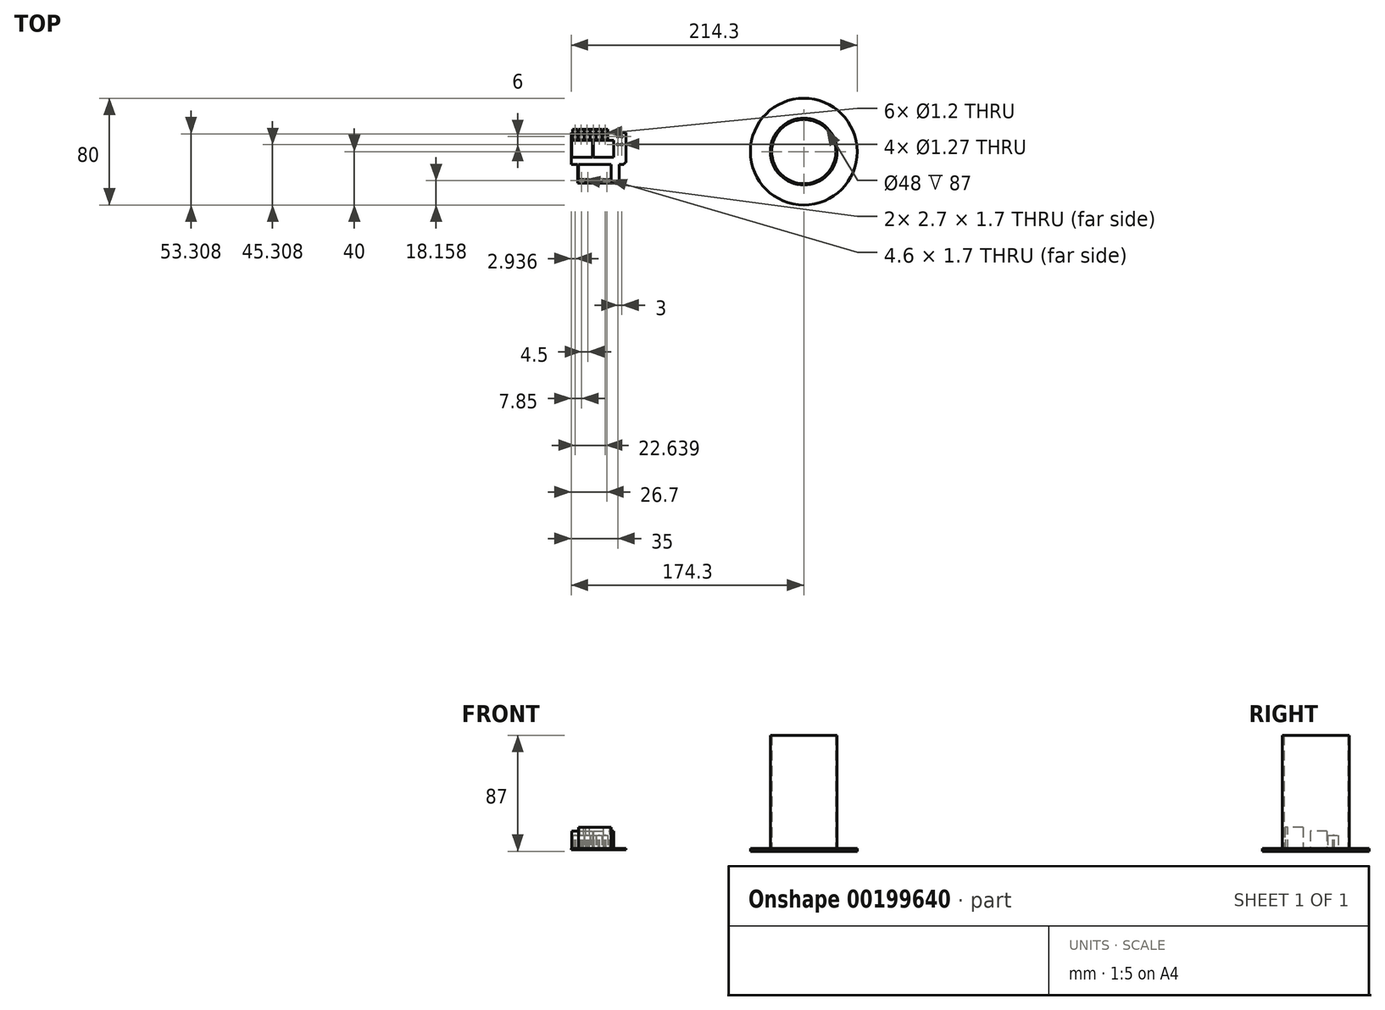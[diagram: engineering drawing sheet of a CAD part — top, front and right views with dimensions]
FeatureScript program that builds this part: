
annotation { "Feature Type Name" : "Feature", "Feature Type Description" : "" }
export const myFeature = defineFeature(function(context is Context, id is Id, definition is map)
    precondition{}
    {
        {
            var Q0;
            Q0=qCreatedBy(makeId("Top.planeOp"),FACE);
            var sketch = newSketch(context, id + "F0", { "sketchPlane" : qUnion([Q0])});
            skCircle(sketch, "E0", {"center": v(0, 0) * mm, "radius": 25 * mm});
            skCircle(sketch, "E1", {"center": v(0, 0) * mm, "radius": 24 * mm});
            skCircle(sketch, "E2", {"center": v(0, 0) * mm, "radius": 40 * mm});
            skSolve(sketch);
        }
        {
            var Q0;
            Q0=makeQuery(id+"F0.imprint","IMPRINT",FACE,{"disambiguationData":[TD([[makeQuery(id+"F0.imprint","IMPRINT",EDGE,{"derivedFrom":sQuery(id+"F0.wireOp",EDGE,"E0")}),1.0]])]});
            extrude(context, id + "F1", {"entities" : qUnion([Q0]), "depth" : 85 * mm});
        }
        {
            var Q0;
            Q0=makeQuery(id+"F0.imprint","IMPRINT",FACE,{"disambiguationData":[TD([[makeQuery(id+"F0.imprint","IMPRINT",EDGE,{"derivedFrom":sQuery(id+"F0.wireOp",EDGE,"E0")}),-1.0]])]});
            var Q1;
            Q1=makeQuery(id+"F0.imprint","IMPRINT",FACE,{"disambiguationData":[TD([[makeQuery(id+"F0.imprint","IMPRINT",EDGE,{"derivedFrom":sQuery(id+"F0.wireOp",EDGE,"E0")}),1.0]])]});
            extrude(context, id + "F2", {"entities" : qUnion([Q0, Q1]), "operationType" : NewBodyOperationType.ADD, "oppositeDirection" : true, "depth" : 2 * mm});
        }
        {
            var Q0;
            Q0=qCreatedBy(makeId("Top.planeOp"),FACE);
            var sketch = newSketch(context, id + "F3", { "sketchPlane" : qUnion([Q0])});
            skLineSegment(sketch, "E3.bottom", {"start": v(-174.3, 14.3) * mm, "end": v(-133.3, 14.3) * mm});
            skLineSegment(sketch, "E3.top", {"start": v(-169.3, -23.7) * mm, "end": v(-138.3, -23.7) * mm});
            skLineSegment(sketch, "E3.left", {"start": v(-174.3, 14.3) * mm, "end": v(-174.3, -9.7) * mm});
            skLineSegment(sketch, "E3.right", {"start": v(-133.3, 14.3) * mm, "end": v(-133.3, -8.2) * mm});
            skLineSegment(sketch, "E4.left", {"start": v(-169.3, -9.7) * mm, "end": v(-169.3, -23.7) * mm});
            skLineSegment(sketch, "E4.right", {"start": v(-138.3, -9.7) * mm, "end": v(-138.3, -23.7) * mm});
            skLineSegment(sketch, "E5", {"start": v(-169.3, -9.7) * mm, "end": v(-174.3, -9.7) * mm});
            skLineSegment(sketch, "E6", {"start": v(-138.3, -9.7) * mm, "end": v(-134.8, -9.7) * mm});
            skLineSegment(sketch, "E7.bottom", {"start": v(-173.8, 8.3) * mm, "end": v(-158.3, 8.3) * mm});
            skLineSegment(sketch, "E7.top", {"start": v(-173.8, -4.2) * mm, "end": v(-158.3, -4.2) * mm});
            skLineSegment(sketch, "E7.left", {"start": v(-173.8, 8.3) * mm, "end": v(-173.8, -4.2) * mm});
            skLineSegment(sketch, "E7.right", {"start": v(-158.3, 8.3) * mm, "end": v(-158.3, -4.2) * mm});
            skLineSegment(sketch, "E8.bottom", {"start": v(-157.8, 8.3) * mm, "end": v(-142.3, 8.3) * mm});
            skLineSegment(sketch, "E8.top", {"start": v(-157.8, -4.2) * mm, "end": v(-142.3, -4.2) * mm});
            skLineSegment(sketch, "E8.left", {"start": v(-157.8, 8.3) * mm, "end": v(-157.8, -4.2) * mm});
            skLineSegment(sketch, "E8.right", {"start": v(-142.3, 8.3) * mm, "end": v(-142.3, -4.2) * mm});
            skCircle(sketch, "E9", {"center": v(-139.3, 11.3) * mm, "radius": 0.64 * mm});
            skCircle(sketch, "E10", {"center": v(-136.3, 11.3) * mm, "radius": 0.64 * mm});
            skCircle(sketch, "E11", {"center": v(-139.3, 5.3) * mm, "radius": 0.64 * mm});
            skCircle(sketch, "E12", {"center": v(-136.3, 5.3) * mm, "radius": 0.64 * mm});
            skLineSegment(sketch, "E13.bottom", {"start": v(-168.8, -9.7) * mm, "end": v(-144.3, -9.7) * mm});
            skLineSegment(sketch, "E13.top", {"start": v(-168.8, -23.2) * mm, "end": v(-144.3, -23.2) * mm});
            skLineSegment(sketch, "E13.left", {"start": v(-168.8, -9.7) * mm, "end": v(-168.8, -23.2) * mm});
            skLineSegment(sketch, "E13.right", {"start": v(-144.3, -9.7) * mm, "end": v(-144.3, -23.2) * mm});
            skLineSegment(sketch, "E14.bottom", {"start": v(-167.8, -21) * mm, "end": v(-165.1, -21) * mm});
            skLineSegment(sketch, "E14.top", {"start": v(-167.8, -22.7) * mm, "end": v(-165.1, -22.7) * mm});
            skLineSegment(sketch, "E14.left", {"start": v(-167.8, -21) * mm, "end": v(-167.8, -22.7) * mm});
            skLineSegment(sketch, "E14.right", {"start": v(-165.1, -21) * mm, "end": v(-165.1, -22.7) * mm});
            skLineSegment(sketch, "E15.bottom", {"start": v(-163.3, -21) * mm, "end": v(-160.6, -21) * mm});
            skLineSegment(sketch, "E15.top", {"start": v(-163.3, -22.7) * mm, "end": v(-160.6, -22.7) * mm});
            skLineSegment(sketch, "E15.left", {"start": v(-163.3, -21) * mm, "end": v(-163.3, -22.7) * mm});
            skLineSegment(sketch, "E15.right", {"start": v(-160.6, -21) * mm, "end": v(-160.6, -22.7) * mm});
            skLineSegment(sketch, "E16.bottom", {"start": v(-149.9, -21) * mm, "end": v(-145.3, -21) * mm});
            skLineSegment(sketch, "E16.top", {"start": v(-149.9, -22.7) * mm, "end": v(-145.3, -22.7) * mm});
            skLineSegment(sketch, "E16.left", {"start": v(-149.9, -21) * mm, "end": v(-149.9, -22.7) * mm});
            skLineSegment(sketch, "E16.right", {"start": v(-145.3, -21) * mm, "end": v(-145.3, -22.7) * mm});
            skLineSegment(sketch, "E17.bottom", {"start": v(-173.8, 16.8) * mm, "end": v(-146.8, 16.8) * mm});
            skLineSegment(sketch, "E17.top", {"start": v(-173.8, 8.8) * mm, "end": v(-146.8, 8.8) * mm});
            skLineSegment(sketch, "E17.left", {"start": v(-173.8, 16.8) * mm, "end": v(-173.8, 8.8) * mm});
            skLineSegment(sketch, "E18.bottom", {"start": v(-169.3, 16.8) * mm, "end": v(-168.8, 16.8) * mm});
            skLineSegment(sketch, "E18.top", {"start": v(-169.3, 8.8) * mm, "end": v(-168.8, 8.8) * mm});
            skLineSegment(sketch, "E18.left", {"start": v(-169.3, 16.8) * mm, "end": v(-169.3, 8.8) * mm});
            skLineSegment(sketch, "E18.right", {"start": v(-168.8, 16.8) * mm, "end": v(-168.8, 8.8) * mm});
            skLineSegment(sketch, "E19.bottom", {"start": v(-164.8, 16.8) * mm, "end": v(-164.3, 16.8) * mm});
            skLineSegment(sketch, "E19.top", {"start": v(-164.8, 8.8) * mm, "end": v(-164.3, 8.8) * mm});
            skLineSegment(sketch, "E19.left", {"start": v(-164.8, 16.8) * mm, "end": v(-164.8, 8.8) * mm});
            skLineSegment(sketch, "E19.right", {"start": v(-164.3, 16.8) * mm, "end": v(-164.3, 8.8) * mm});
            skLineSegment(sketch, "E20.top", {"start": v(-160.3, 8.8) * mm, "end": v(-159.8, 8.8) * mm});
            skLineSegment(sketch, "E21.bottom", {"start": v(-155.8, 16.8) * mm, "end": v(-155.3, 16.8) * mm});
            skLineSegment(sketch, "E21.top", {"start": v(-155.8, 8.8) * mm, "end": v(-155.3, 8.8) * mm});
            skLineSegment(sketch, "E21.left", {"start": v(-155.8, 16.8) * mm, "end": v(-155.8, 8.8) * mm});
            skLineSegment(sketch, "E21.right", {"start": v(-155.3, 16.8) * mm, "end": v(-155.3, 8.8) * mm});
            skLineSegment(sketch, "E22.bottom", {"start": v(-151.3, 16.8) * mm, "end": v(-150.8, 16.8) * mm});
            skLineSegment(sketch, "E22.top", {"start": v(-151.3, 8.8) * mm, "end": v(-150.8, 8.8) * mm});
            skLineSegment(sketch, "E22.left", {"start": v(-151.3, 16.8) * mm, "end": v(-151.3, 8.8) * mm});
            skLineSegment(sketch, "E22.right", {"start": v(-150.8, 16.8) * mm, "end": v(-150.8, 8.8) * mm});
            skLineSegment(sketch, "E23", {"start": v(-173.3, 16.8) * mm, "end": v(-173.3, 8.8) * mm});
            skLineSegment(sketch, "E24", {"start": v(-146.8, 16.8) * mm, "end": v(-146.8, 8.8) * mm});
            skLineSegment(sketch, "E25.bottom", {"start": v(-146.8, 16.8) * mm, "end": v(-146.3, 16.8) * mm});
            skLineSegment(sketch, "E25.right", {"start": v(-146.3, 16.8) * mm, "end": v(-146.3, 8.8) * mm});
            skCircle(sketch, "E26", {"center": v(-171.36, 13.3) * mm, "radius": 0.6 * mm});
            skCircle(sketch, "E27", {"center": v(-166.8, 13.3) * mm, "radius": 0.6 * mm});
            skCircle(sketch, "E28", {"center": v(-162.34, 13.3) * mm, "radius": 0.6 * mm});
            skCircle(sketch, "E29", {"center": v(-148.73, 13.3) * mm, "radius": 0.6 * mm});
            skCircle(sketch, "E30", {"center": v(-157.7, 13.3) * mm, "radius": 0.6 * mm});
            skCircle(sketch, "E31", {"center": v(-153.36, 13.3) * mm, "radius": 0.6 * mm});
            skLineSegment(sketch, "E32", {"start": v(-160.3, 8.8) * mm, "end": v(-160.3, 16.8) * mm});
            skLineSegment(sketch, "E33", {"start": v(-159.8, 8.8) * mm, "end": v(-159.8, 16.8) * mm});
            skLineSegment(sketch, "E34", {"start": v(-146.8, 8.8) * mm, "end": v(-146.3, 8.8) * mm});
            skArc(sketch, "E35", {"start": v(-133.3, -8.2) * mm, "mid": v(-134.36, -8.63) * mm, "end": v(-134.8, -9.7) * mm});
            skSolve(sketch);
        }
        {
            var Q0;
            Q0=makeQuery(id+"F3.imprint","IMPRINT",FACE,{"disambiguationData":[TD([[makeQuery(id+"F3.imprint","IMPRINT",EDGE,{"derivedFrom":sQuery(id+"F3.wireOp",EDGE,"E26")}),-1.0]])]});
            var Q1;
            Q1=makeQuery(id+"F3.imprint","IMPRINT",FACE,{"disambiguationData":[TD([[makeQuery(id+"F3.imprint","IMPRINT",EDGE,{"derivedFrom":sQuery(id+"F3.wireOp",EDGE,"E27")}),-1.0]])]});
            var Q2;
            Q2=makeQuery(id+"F3.imprint","IMPRINT",FACE,{"disambiguationData":[TD([[makeQuery(id+"F3.imprint","IMPRINT",EDGE,{"derivedFrom":sQuery(id+"F3.wireOp",EDGE,"E28")}),-1.0]])]});
            var Q3;
            Q3=makeQuery(id+"F3.imprint","IMPRINT",FACE,{"disambiguationData":[TD([[makeQuery(id+"F3.imprint","IMPRINT",EDGE,{"derivedFrom":sQuery(id+"F3.wireOp",EDGE,"E30")}),-1.0]])]});
            var Q4;
            Q4=makeQuery(id+"F3.imprint","IMPRINT",FACE,{"disambiguationData":[TD([[makeQuery(id+"F3.imprint","IMPRINT",EDGE,{"derivedFrom":sQuery(id+"F3.wireOp",EDGE,"E31")}),-1.0]])]});
            var Q5;
            Q5=makeQuery(id+"F3.imprint","IMPRINT",FACE,{"disambiguationData":[TD([[makeQuery(id+"F3.imprint","IMPRINT",EDGE,{"derivedFrom":sQuery(id+"F3.wireOp",EDGE,"E29")}),-1.0]])]});
            var Q6;
            Q6=makeQuery(id+"F3.imprint","IMPRINT",FACE,{"disambiguationData":[TD([[makeQuery(id+"F3.imprint","IMPRINT",EDGE,{"derivedFrom":sQuery(id+"F3.wireOp",EDGE,"E7.bottom")}),-1.0]])]});
            var Q7;
            Q7=makeQuery(id+"F3.imprint","IMPRINT",FACE,{"disambiguationData":[TD([[makeQuery(id+"F3.imprint","IMPRINT",EDGE,{"derivedFrom":sQuery(id+"F3.wireOp",EDGE,"E8.bottom")}),-1.0]])]});
            var Q8;
            Q8=makeQuery(id+"F3.imprint","IMPRINT",FACE,{"disambiguationData":[TD([[makeQuery(id+"F3.imprint","IMPRINT",EDGE,{"derivedFrom":sQuery(id+"F3.wireOp",EDGE,"E13.bottom")}),-1.0]])]});
            var Q9;
            {var subQ0=sQuery(id+"F3.wireOp",EDGE,"E17.left");var subQ1=sQuery(id+"F3.wireOp",EDGE,"E3.bottom");var subQ2=makeQuery(id+"F3.imprint","INTERSECT",VERTEX,{"derivedFrom":[subQ1,subQ0]});Q9=makeQuery(id+"F3.imprint","IMPRINT",FACE,{"disambiguationData":[TD([[makeQuery(id+"F3.imprint","IMPRINT",EDGE,{"disambiguationData":[TD([[subQ2,-1.0]])],"derivedFrom":subQ1}),-1.0]])]});}
            var Q10;
            {var subQ0=sQuery(id+"F3.wireOp",EDGE,"E18.left");var subQ1=sQuery(id+"F3.wireOp",EDGE,"E3.bottom");var subQ2=makeQuery(id+"F3.imprint","INTERSECT",VERTEX,{"derivedFrom":[subQ1,subQ0]});Q10=makeQuery(id+"F3.imprint","IMPRINT",FACE,{"disambiguationData":[TD([[makeQuery(id+"F3.imprint","IMPRINT",EDGE,{"disambiguationData":[TD([[subQ2,-1.0]])],"derivedFrom":subQ1}),-1.0]])]});}
            var Q11;
            {var subQ0=sQuery(id+"F3.wireOp",EDGE,"E19.right");var subQ1=sQuery(id+"F3.wireOp",EDGE,"E3.bottom");var subQ2=makeQuery(id+"F3.imprint","INTERSECT",VERTEX,{"derivedFrom":[subQ1,subQ0]});Q11=makeQuery(id+"F3.imprint","IMPRINT",FACE,{"disambiguationData":[TD([[makeQuery(id+"F3.imprint","IMPRINT",EDGE,{"disambiguationData":[TD([[subQ2,1.0]])],"derivedFrom":subQ1}),-1.0]])]});}
            var Q12;
            {var subQ0=sQuery(id+"F3.wireOp",EDGE,"E33");var subQ1=sQuery(id+"F3.wireOp",EDGE,"E3.bottom");var subQ2=makeQuery(id+"F3.imprint","INTERSECT",VERTEX,{"derivedFrom":[subQ1,subQ0]});Q12=makeQuery(id+"F3.imprint","IMPRINT",FACE,{"disambiguationData":[TD([[makeQuery(id+"F3.imprint","IMPRINT",EDGE,{"disambiguationData":[TD([[subQ2,1.0]])],"derivedFrom":subQ1}),-1.0]])]});}
            var Q13;
            {var subQ0=sQuery(id+"F3.wireOp",EDGE,"E21.left");var subQ1=sQuery(id+"F3.wireOp",EDGE,"E3.bottom");var subQ2=makeQuery(id+"F3.imprint","INTERSECT",VERTEX,{"derivedFrom":[subQ1,subQ0]});Q13=makeQuery(id+"F3.imprint","IMPRINT",FACE,{"disambiguationData":[TD([[makeQuery(id+"F3.imprint","IMPRINT",EDGE,{"disambiguationData":[TD([[subQ2,-1.0]])],"derivedFrom":subQ1}),-1.0]])]});}
            var Q14;
            {var subQ0=sQuery(id+"F3.wireOp",EDGE,"E22.left");var subQ1=sQuery(id+"F3.wireOp",EDGE,"E3.bottom");var subQ2=makeQuery(id+"F3.imprint","INTERSECT",VERTEX,{"derivedFrom":[subQ1,subQ0]});Q14=makeQuery(id+"F3.imprint","IMPRINT",FACE,{"disambiguationData":[TD([[makeQuery(id+"F3.imprint","IMPRINT",EDGE,{"disambiguationData":[TD([[subQ2,-1.0]])],"derivedFrom":subQ1}),-1.0]])]});}
            var Q15;
            Q15=makeQuery(id+"F3.imprint","IMPRINT",FACE,{"disambiguationData":[TD([[makeQuery(id+"F3.imprint","IMPRINT",EDGE,{"derivedFrom":sQuery(id+"F3.wireOp",EDGE,"E3.top")}),1.0]])]});
            var Q16;
            {var subQ5=sQuery(id+"F3.wireOp",EDGE,"E34");Q16=makeQuery(id+"F3.imprint","IMPRINT",FACE,{"disambiguationData":[TD([[makeQuery(id+"F3.imprint","IMPRINT",EDGE,{"derivedFrom":subQ5}),1.0]])]});}
            extrude(context, id + "F4", {"entities" : qUnion([Q0, Q1, Q2, Q3, Q4, Q5, Q6, Q7, Q8, Q9, Q10, Q11, Q12, Q13, Q14, Q15, Q16]), "oppositeDirection" : true, "depth" : 0.8 * mm, "offsetDistance" : 25 * mm});
        }
        {
            var Q0;
            Q0=makeQuery(id+"F3.imprint","IMPRINT",FACE,{"disambiguationData":[TD([[makeQuery(id+"F3.imprint","IMPRINT",EDGE,{"derivedFrom":sQuery(id+"F3.wireOp",EDGE,"E7.bottom")}),-1.0]])]});
            var Q1;
            Q1=makeQuery(id+"F3.imprint","IMPRINT",FACE,{"disambiguationData":[TD([[makeQuery(id+"F3.imprint","IMPRINT",EDGE,{"derivedFrom":sQuery(id+"F3.wireOp",EDGE,"E8.bottom")}),-1.0]])]});
            extrude(context, id + "F5", {"entities" : qUnion([Q0, Q1]), "operationType" : NewBodyOperationType.ADD, "depth" : 13 * mm, "offsetDistance" : 25 * mm});
        }
        {
            var Q0;
            Q0=makeQuery(id+"F3.imprint","IMPRINT",FACE,{"disambiguationData":[TD([[makeQuery(id+"F3.imprint","IMPRINT",EDGE,{"derivedFrom":sQuery(id+"F3.wireOp",EDGE,"E26")}),-1.0]])]});
            var Q1;
            {var subQ0=sQuery(id+"F3.wireOp",EDGE,"E18.left");var subQ1=sQuery(id+"F3.wireOp",EDGE,"E3.bottom");var subQ2=makeQuery(id+"F3.imprint","INTERSECT",VERTEX,{"derivedFrom":[subQ1,subQ0]});Q1=makeQuery(id+"F3.imprint","IMPRINT",FACE,{"disambiguationData":[TD([[makeQuery(id+"F3.imprint","IMPRINT",EDGE,{"disambiguationData":[TD([[subQ2,1.0]])],"derivedFrom":subQ1}),1.0]])]});}
            var Q2;
            {var subQ0=sQuery(id+"F3.wireOp",EDGE,"E18.right");var subQ1=sQuery(id+"F3.wireOp",EDGE,"E3.bottom");var subQ2=makeQuery(id+"F3.imprint","INTERSECT",VERTEX,{"derivedFrom":[subQ1,subQ0]});Q2=makeQuery(id+"F3.imprint","IMPRINT",FACE,{"disambiguationData":[TD([[makeQuery(id+"F3.imprint","IMPRINT",EDGE,{"disambiguationData":[TD([[subQ2,-1.0]])],"derivedFrom":subQ1}),1.0]])]});}
            var Q3;
            Q3=makeQuery(id+"F3.imprint","IMPRINT",FACE,{"disambiguationData":[TD([[makeQuery(id+"F3.imprint","IMPRINT",EDGE,{"derivedFrom":sQuery(id+"F3.wireOp",EDGE,"E27")}),-1.0]])]});
            var Q4;
            {var subQ0=sQuery(id+"F3.wireOp",EDGE,"E19.right");var subQ1=sQuery(id+"F3.wireOp",EDGE,"E3.bottom");var subQ2=makeQuery(id+"F3.imprint","INTERSECT",VERTEX,{"derivedFrom":[subQ1,subQ0]});Q4=makeQuery(id+"F3.imprint","IMPRINT",FACE,{"disambiguationData":[TD([[makeQuery(id+"F3.imprint","IMPRINT",EDGE,{"disambiguationData":[TD([[subQ2,-1.0]])],"derivedFrom":subQ1}),1.0]])]});}
            var Q5;
            Q5=makeQuery(id+"F3.imprint","IMPRINT",FACE,{"disambiguationData":[TD([[makeQuery(id+"F3.imprint","IMPRINT",EDGE,{"derivedFrom":sQuery(id+"F3.wireOp",EDGE,"E28")}),-1.0]])]});
            var Q6;
            Q6=makeQuery(id+"F3.imprint","IMPRINT",FACE,{"disambiguationData":[TD([[makeQuery(id+"F3.imprint","IMPRINT",EDGE,{"derivedFrom":sQuery(id+"F3.wireOp",EDGE,"E30")}),-1.0]])]});
            var Q7;
            {var subQ0=sQuery(id+"F3.wireOp",EDGE,"E21.left");var subQ1=sQuery(id+"F3.wireOp",EDGE,"E3.bottom");var subQ2=makeQuery(id+"F3.imprint","INTERSECT",VERTEX,{"derivedFrom":[subQ1,subQ0]});Q7=makeQuery(id+"F3.imprint","IMPRINT",FACE,{"disambiguationData":[TD([[makeQuery(id+"F3.imprint","IMPRINT",EDGE,{"disambiguationData":[TD([[subQ2,1.0]])],"derivedFrom":subQ1}),1.0]])]});}
            var Q8;
            Q8=makeQuery(id+"F3.imprint","IMPRINT",FACE,{"disambiguationData":[TD([[makeQuery(id+"F3.imprint","IMPRINT",EDGE,{"derivedFrom":sQuery(id+"F3.wireOp",EDGE,"E31")}),-1.0]])]});
            var Q9;
            {var subQ0=sQuery(id+"F3.wireOp",EDGE,"E21.right");var subQ1=sQuery(id+"F3.wireOp",EDGE,"E3.bottom");var subQ2=makeQuery(id+"F3.imprint","INTERSECT",VERTEX,{"derivedFrom":[subQ1,subQ0]});Q9=makeQuery(id+"F3.imprint","IMPRINT",FACE,{"disambiguationData":[TD([[makeQuery(id+"F3.imprint","IMPRINT",EDGE,{"disambiguationData":[TD([[subQ2,-1.0]])],"derivedFrom":subQ1}),1.0]])]});}
            var Q10;
            {var subQ0=sQuery(id+"F3.wireOp",EDGE,"E22.right");var subQ1=sQuery(id+"F3.wireOp",EDGE,"E3.bottom");var subQ2=makeQuery(id+"F3.imprint","INTERSECT",VERTEX,{"derivedFrom":[subQ1,subQ0]});Q10=makeQuery(id+"F3.imprint","IMPRINT",FACE,{"disambiguationData":[TD([[makeQuery(id+"F3.imprint","IMPRINT",EDGE,{"disambiguationData":[TD([[subQ2,-1.0]])],"derivedFrom":subQ1}),1.0]])]});}
            var Q11;
            Q11=makeQuery(id+"F3.imprint","IMPRINT",FACE,{"disambiguationData":[TD([[makeQuery(id+"F3.imprint","IMPRINT",EDGE,{"derivedFrom":sQuery(id+"F3.wireOp",EDGE,"E29")}),-1.0]])]});
            extrude(context, id + "F6", {"entities" : qUnion([Q0, Q1, Q2, Q3, Q4, Q5, Q6, Q7, Q8, Q9, Q10, Q11]), "operationType" : NewBodyOperationType.ADD, "depth" : 10 * mm, "offsetDistance" : 25 * mm});
        }
        {
            var Q0;
            Q0=makeQuery(id+"F3.imprint","IMPRINT",FACE,{"disambiguationData":[TD([[makeQuery(id+"F3.imprint","IMPRINT",EDGE,{"derivedFrom":sQuery(id+"F3.wireOp",EDGE,"E13.bottom")}),-1.0]])]});
            extrude(context, id + "F7", {"entities" : qUnion([Q0]), "operationType" : NewBodyOperationType.ADD, "depth" : 16 * mm, "offsetDistance" : 25 * mm});
        }
        {
            var Q0;
            Q0=makeQuery(id+"F7.opExtrude","SWEPT_FACE",FACE,{"disambiguationData":[OSD([sQuery(id+"F3.wireOp",EDGE,"E13.right")])]});
            var sketch = newSketch(context, id + "F8", { "sketchPlane" : qUnion([Q0])});
            skLineSegment(sketch, "E36", {"start": v(-20.2, 0) * mm, "end": v(-20.2, 0.7) * mm});
            skLineSegment(sketch, "E37", {"start": v(-20.2, 0.7) * mm, "end": v(-9.7, 0.7) * mm});
            skLineSegment(sketch, "E38", {"start": v(-9.7, 0.7) * mm, "end": v(-9.7, 0) * mm});
            skLineSegment(sketch, "E39", {"start": v(-9.7, 0) * mm, "end": v(-20.2, 0) * mm});
            skSolve(sketch);
        }
        {
            var Q0;
            Q0=makeQuery(id+"F8.imprint","IMPRINT",FACE,{"disambiguationData":[TD([[makeQuery(id+"F8.imprint","IMPRINT",EDGE,{"derivedFrom":sQuery(id+"F8.wireOp",EDGE,"E36")}),-1.0]])]});
            extrude(context, id + "F9", {"entities" : qUnion([Q0]), "operationType" : NewBodyOperationType.REMOVE, "oppositeDirection" : true, "depth" : 25 * mm, "offsetDistance" : 25 * mm});
        }
    });
